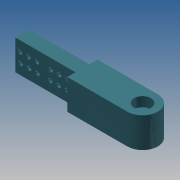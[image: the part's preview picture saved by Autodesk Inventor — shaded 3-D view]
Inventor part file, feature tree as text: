
AUTODESK INVENTOR PART (.ipt)
format: ipt  version: 2013 (Build 170138000, 138)  size: 172,032 bytes
history: native  units: mm
features: extrude x8, sketch x8, fillet x1
ambient origin geometry x8: Origin, YZ Plane, XZ Plane, XY Plane, X Axis, Y Axis, Z Axis, Center Point
bodies: Solid1 (feature_tree)
feature tree (17):
  extrude  "Extrusion1"  Depth=12.6mm
  extrude  "Extrusion2"  Depth=8.5mm
  extrude  "Extrusion3"  Depth=22.0mm
  extrude  "Extrusion4"  Depth=20.0mm
  extrude  "Extrusion5"  Depth=7.0mm TaperAngle=0.0deg
  extrude  "Extrusion6"  Depth=3.5mm
  fillet  "Fillet1"  Radius=35.0mm
  extrude  "Extrusion7"  Depth=6.0mm
  extrude  "Extrusion8"  Depth=8.0mm TaperAngle=0.0deg
  sketch  "Sketch1"  dims[d0=150.0mm d2=12.6mm]
  sketch  "Sketch2"  dims[d3=15.0mm d4=8.5mm]
  sketch  "Sketch4"  dims[d5=25.0mm d6=0.0mm d7=22.0mm]
  sketch  "Sketch5"  dims[d9=7.0mm d10=0.0mm d16=20.0mm]
  sketch  "Sketch6"  dims[d17=40.0mm d18=7.0mm d19=0.0mm]
  sketch  "Sketch7"  dims[d21=3.0mm d22=0.0mm d23=3.5mm d24=35.0mm]
  sketch  "Sketch8"  dims[d26=10.0mm d27=0.0mm d28=6.0mm]
  sketch  "Sketch9"  dims[d30=14.0mm d32=8.0mm d33=0.0mm d34=3.5mm d35=50.0mm d36=50.0mm d37=11.5mm d38=10.0mm d39=0.0mm d40=12.5mm d41=8.0mm d42=0.5mm d43=1.0mm d44=1.5mm d45=2.0mm d46=2.5mm d47=3.5mm d48=25.0mm d49=0.5mm d50=1.0mm d51=1.5mm d52=2.0mm d53=2.5mm d54=10.0mm d55=0.0mm]
